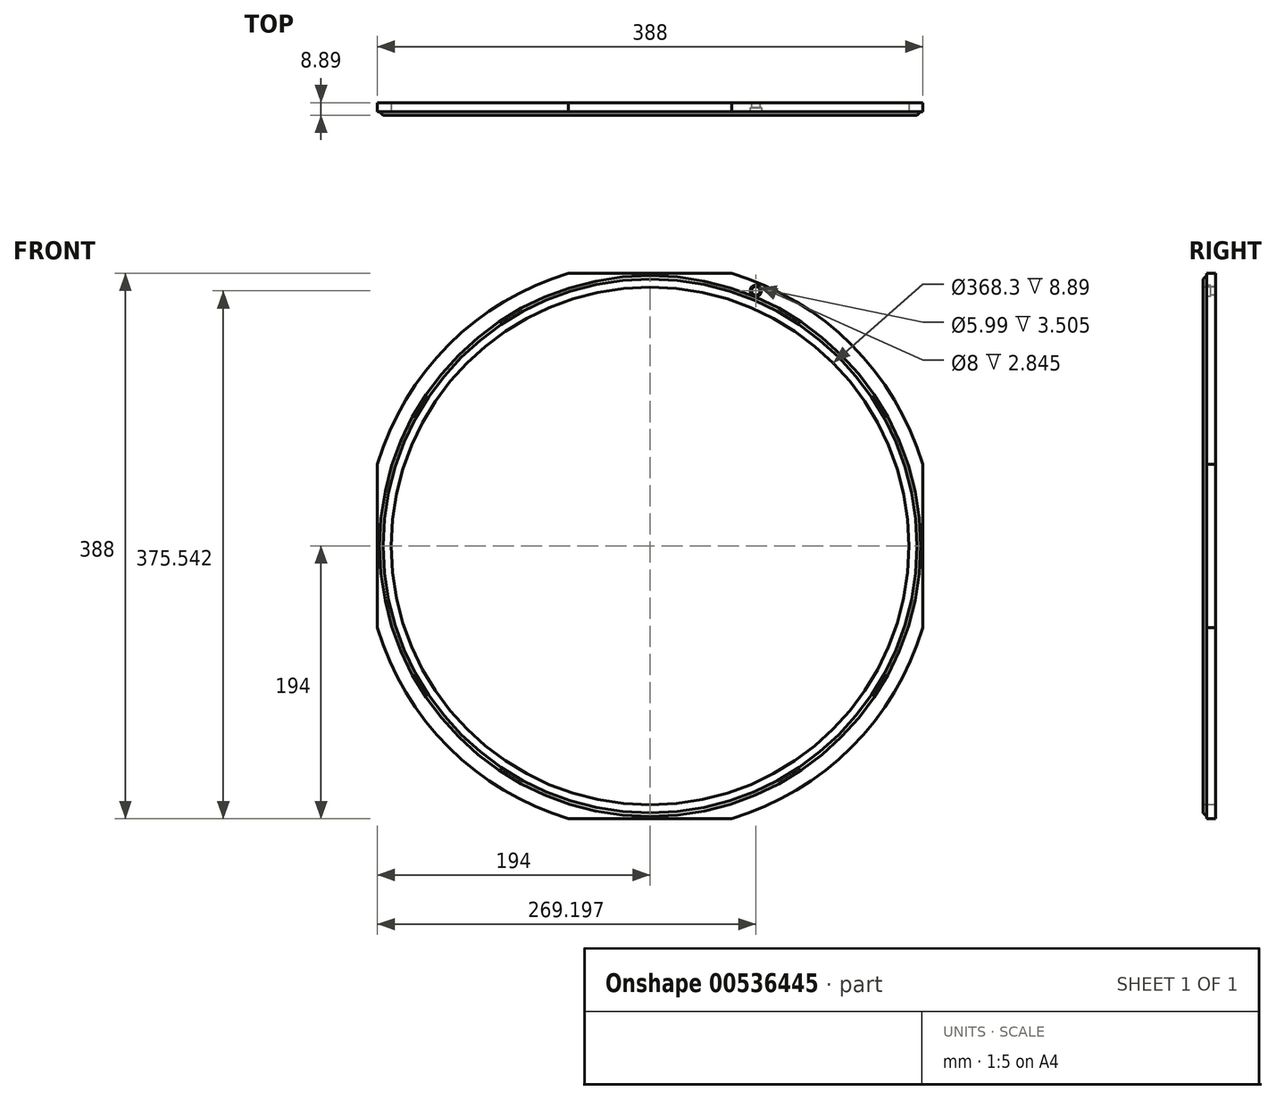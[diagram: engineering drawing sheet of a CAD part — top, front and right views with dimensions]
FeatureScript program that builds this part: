
annotation { "Feature Type Name" : "Feature", "Feature Type Description" : "" }
export const myFeature = defineFeature(function(context is Context, id is Id, definition is map)
    precondition{}
    {
        {
            var Q0;
            Q0=qCreatedBy(makeId("Right.planeOp"),FACE);
            var sketch = newSketch(context, id + "F0", { "sketchPlane" : qUnion([Q0])});
            skLineSegment(sketch, "E0", {"start": v(0, 0) * mm, "end": v(154.67, 0) * mm, "construction": true});
            skLineSegment(sketch, "E1", {"start": v(0, 184.15) * mm, "end": v(0, 202.5) * mm});
            skLineSegment(sketch, "E2", {"start": v(0, 202.5) * mm, "end": v(-6.35, 202.5) * mm});
            skLineSegment(sketch, "E3", {"start": v(-6.35, 202.5) * mm, "end": v(-6.35, 192.34) * mm});
            skLineSegment(sketch, "E4", {"start": v(-6.35, 192.34) * mm, "end": v(-8.9, 189.8) * mm});
            skLineSegment(sketch, "E5", {"start": v(-8.89, 189.8) * mm, "end": v(-8.89, 184.15) * mm});
            skLineSegment(sketch, "E6", {"start": v(-8.89, 184.15) * mm, "end": v(0, 184.15) * mm});
            skSolve(sketch);
        }
        {
            var Q0;
            Q0 = qSketchRegion(id + "F0", true);
            var Q1;
            Q1=sQuery(id+"F0.wireOp",EDGE,"E0");
            revolve(context, id + "F1", {"entities" : qUnion([Q0]), "axis" : qUnion([Q1]), "revolveType" : RevolveType.FULL});
        }
        {
            var Q0;
            Q0=makeQuery(id+"F1.opRevolve","SWEPT_FACE",FACE,{"disambiguationData":[OSD([sQuery(id+"F0.wireOp",EDGE,"E3")])]});
            var sketch = newSketch(context, id + "F2", { "sketchPlane" : qUnion([Q0])});
            skPoint(sketch, "E7", {"position": v(75.2, 181.54) * mm});
            skLineSegment(sketch, "E8", {"start": v(75.2, 181.54) * mm, "end": v(0, 0) * mm, "construction": true});
            skLineSegment(sketch, "E9", {"start": v(0, 0) * mm, "end": v(0, 185.91) * mm, "construction": true});
            skCircle(sketch, "E10", {"center": v(0, 0) * mm, "radius": 196.5 * mm, "construction": true});
            skSolve(sketch);
        }
        {
            var Q0;
            Q0=sQuery(id+"F2.wireOp",VERTEX,"E7");
            var Q1;
            Q1=makeQuery(id+"F1.opRevolve","SWEPT_BODY",BODY,{"disambiguationData":[OSD([sQuery(id+"F0.wireOp",EDGE,"E1"),sQuery(id+"F0.wireOp",EDGE,"E2"),sQuery(id+"F0.wireOp",EDGE,"E3"),sQuery(id+"F0.wireOp",EDGE,"E4"),sQuery(id+"F0.wireOp",EDGE,"E5"),sQuery(id+"F0.wireOp",EDGE,"E6")])]});
            hole(context, id + "F3", {"style" : HoleStyle.C_BORE, "endStyle" : HoleEndStyle.BLIND, "holeDiameter" : 6 * mm, "cBoreDiameter" : 8 * mm, "cBoreDepth" : 2.84 * mm, "holeDepth" : 25.4 * mm, "isTappedThrough" : true, "tappedDepth" : 12.7 * mm, "tapClearance" : 3, "startFromSketch" : true, "locations" : qUnion([Q0]), "scope" : qUnion([Q1])});
        }
        {
            var Q0;
            Q0=makeQuery(id+"F1.opRevolve","SWEPT_FACE",FACE,{"disambiguationData":[OSD([sQuery(id+"F0.wireOp",EDGE,"E3")])]});
            var sketch = newSketch(context, id + "F4", { "sketchPlane" : qUnion([Q0])});
            skLineSegment(sketch, "E11.bottom", {"start": v(194, 194) * mm, "end": v(-194, 194) * mm});
            skLineSegment(sketch, "E11.top", {"start": v(194, -194) * mm, "end": v(-194, -194) * mm});
            skLineSegment(sketch, "E11.left", {"start": v(194, 194) * mm, "end": v(194, -194) * mm});
            skLineSegment(sketch, "E11.right", {"start": v(-194, 194) * mm, "end": v(-194, -194) * mm});
            skPoint(sketch, "E11.middle", {"position": v(0, 0) * mm});
            skCircle(sketch, "E12", {"center": v(0, 0) * mm, "radius": 365.41 * mm});
            skSolve(sketch);
        }
        {
            var Q0;
            Q0 = qSketchRegion(id + "F4", true);
            extrude(context, id + "F5", {"entities" : qUnion([Q0]), "operationType" : NewBodyOperationType.REMOVE, "endBound" : BoundingType.THROUGH_ALL, "oppositeDirection" : true, "depth" : 25.4 * mm, "offsetDistance" : 25.4 * mm});
        }
    });
